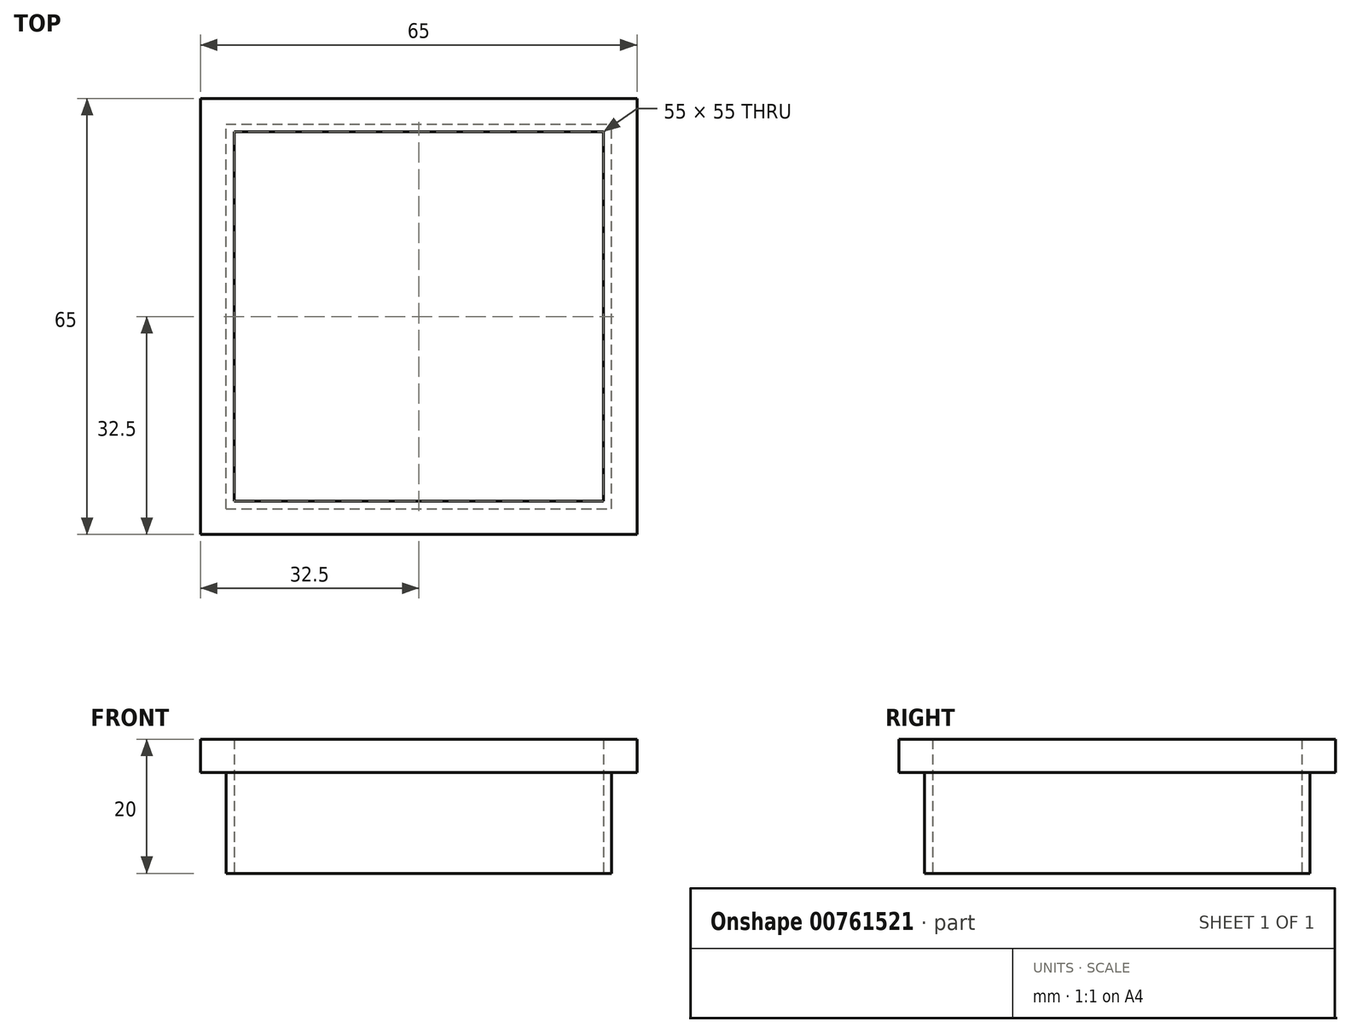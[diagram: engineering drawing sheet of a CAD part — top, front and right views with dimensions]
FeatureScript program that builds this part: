
annotation { "Feature Type Name" : "Feature", "Feature Type Description" : "" }
export const myFeature = defineFeature(function(context is Context, id is Id, definition is map)
    precondition{}
    {
        {
            var Q0;
            Q0=qCreatedBy(makeId("Top.planeOp"),FACE);
            var sketch = newSketch(context, id + "F0", { "sketchPlane" : qUnion([Q0])});
            skLineSegment(sketch, "E0.bottom", {"start": v(0, 0) * mm, "end": v(57.4, 0) * mm});
            skLineSegment(sketch, "E0.top", {"start": v(0, 57.4) * mm, "end": v(57.4, 57.4) * mm});
            skLineSegment(sketch, "E0.left", {"start": v(0, 0) * mm, "end": v(0, 57.4) * mm});
            skLineSegment(sketch, "E0.right", {"start": v(57.4, 0) * mm, "end": v(57.4, 57.4) * mm});
            skLineSegment(sketch, "E1.bottom", {"start": v(1.2, 1.2) * mm, "end": v(56.2, 1.2) * mm});
            skLineSegment(sketch, "E1.top", {"start": v(1.2, 56.2) * mm, "end": v(56.2, 56.2) * mm});
            skLineSegment(sketch, "E1.left", {"start": v(1.2, 1.2) * mm, "end": v(1.2, 56.2) * mm});
            skLineSegment(sketch, "E1.right", {"start": v(56.2, 1.2) * mm, "end": v(56.2, 56.2) * mm});
            skSolve(sketch);
        }
        {
            var Q0;
            Q0=makeQuery(id+"F0.imprint","IMPRINT",FACE,{"disambiguationData":[TD([[makeQuery(id+"F0.imprint","IMPRINT",EDGE,{"derivedFrom":sQuery(id+"F0.wireOp",EDGE,"E0.bottom")}),1.0]])]});
            extrude(context, id + "F1", {"entities" : qUnion([Q0]), "depth" : 20 * mm, "offsetDistance" : 25 * mm});
        }
        {
            var Q0;
            Q0=makeQuery(id+"F1.opExtrude","CAP_FACE",FACE,{"disambiguationData":[OSD([sQuery(id+"F0.wireOp",EDGE,"E0.bottom"),sQuery(id+"F0.wireOp",EDGE,"E0.top"),sQuery(id+"F0.wireOp",EDGE,"E0.left"),sQuery(id+"F0.wireOp",EDGE,"E0.right"),sQuery(id+"F0.wireOp",EDGE,"E1.bottom"),sQuery(id+"F0.wireOp",EDGE,"E1.top"),sQuery(id+"F0.wireOp",EDGE,"E1.left"),sQuery(id+"F0.wireOp",EDGE,"E1.right")])],"isStart":false});
            var sketch = newSketch(context, id + "F2", { "sketchPlane" : qUnion([Q0])});
            skLineSegment(sketch, "E2.bottom", {"start": v(-3.8, 61.2) * mm, "end": v(61.2, 61.2) * mm});
            skLineSegment(sketch, "E2.top", {"start": v(-3.8, -3.8) * mm, "end": v(61.2, -3.8) * mm});
            skLineSegment(sketch, "E2.left", {"start": v(-3.8, 61.2) * mm, "end": v(-3.8, -3.8) * mm});
            skLineSegment(sketch, "E2.right", {"start": v(61.2, 61.2) * mm, "end": v(61.2, -3.8) * mm});
            skSolve(sketch);
        }
        {
            var Q0;
            Q0=makeQuery(id+"F2.imprint","IMPRINT",FACE,{"disambiguationData":[TD([[makeQuery(id+"F2.imprint","IMPRINT",EDGE,{"derivedFrom":sQuery(id+"F2.wireOp",EDGE,"E2.bottom")}),-1.0]])]});
            extrude(context, id + "F3", {"entities" : qUnion([Q0]), "operationType" : NewBodyOperationType.ADD, "oppositeDirection" : true, "depth" : 5 * mm, "offsetDistance" : 25 * mm});
        }
    });
